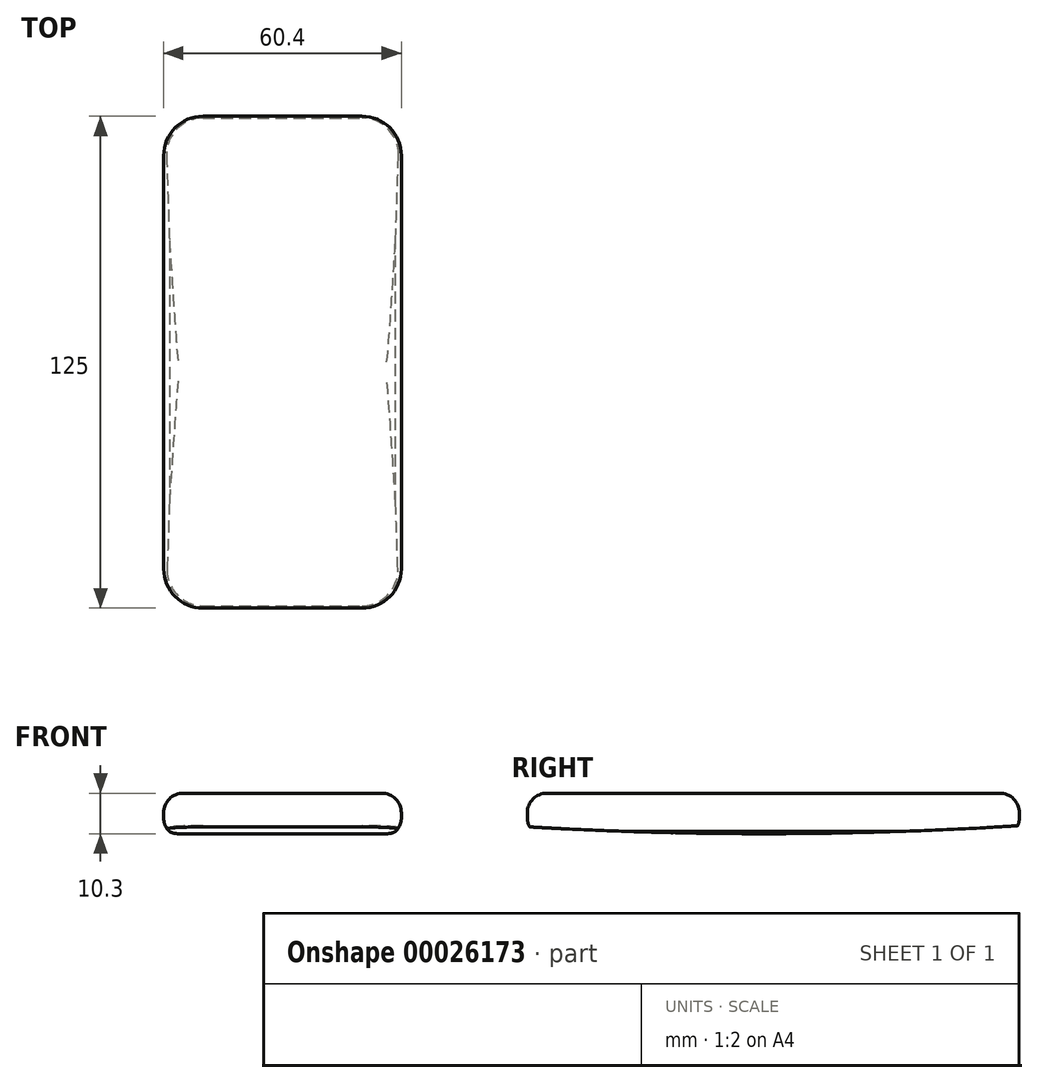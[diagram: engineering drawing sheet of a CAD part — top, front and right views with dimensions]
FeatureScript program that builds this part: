
annotation { "Feature Type Name" : "Feature", "Feature Type Description" : "" }
export const myFeature = defineFeature(function(context is Context, id is Id, definition is map)
    precondition{}
    {
        {
            var Q0;
            Q0=qCreatedBy(makeId("Top.planeOp"),FACE);
            var sketch = newSketch(context, id + "F0", { "sketchPlane" : qUnion([Q0])});
            skLineSegment(sketch, "E0.rect.bottom", {"start": v(-30.2, 62.5) * mm, "end": v(30.2, 62.5) * mm});
            skLineSegment(sketch, "E0.rect.top", {"start": v(-30.2, -62.5) * mm, "end": v(30.2, -62.5) * mm});
            skLineSegment(sketch, "E0.rect.left", {"start": v(-30.2, 62.5) * mm, "end": v(-30.2, -62.5) * mm});
            skLineSegment(sketch, "E0.rect.right", {"start": v(30.2, 62.5) * mm, "end": v(30.2, -62.5) * mm});
            skPoint(sketch, "E0.rect.middle", {"position": v(0, 0) * mm});
            skSolve(sketch);
        }
        {
            var Q0;
            Q0=makeQuery(id+"F0.imprint","IMPRINT",FACE,{"disambiguationData":[TD([[makeQuery(id+"F0.imprint","IMPRINT",EDGE,{"derivedFrom":sQuery(id+"F0.wireOp",EDGE,"E0.rect.bottom")}),-1.0]])]});
            extrude(context, id + "F1", {"entities" : qUnion([Q0]), "depth" : 10.3 * mm});
        }
        {
            var Q0;
            Q0=makeQuery(id+"F1.opExtrude","SWEPT_EDGE",EDGE,{"disambiguationData":[OSD([sQuery(id+"F0.wireOp",EDGE,"E0.rect.bottom"),sQuery(id+"F0.wireOp",EDGE,"E0.rect.left")])]});
            var Q1;
            Q1=makeQuery(id+"F1.opExtrude","SWEPT_EDGE",EDGE,{"disambiguationData":[OSD([sQuery(id+"F0.wireOp",EDGE,"E0.rect.top"),sQuery(id+"F0.wireOp",EDGE,"E0.rect.left")])]});
            var Q2;
            Q2=makeQuery(id+"F1.opExtrude","SWEPT_EDGE",EDGE,{"disambiguationData":[OSD([sQuery(id+"F0.wireOp",EDGE,"E0.rect.top"),sQuery(id+"F0.wireOp",EDGE,"E0.rect.right")])]});
            var Q3;
            Q3=makeQuery(id+"F1.opExtrude","SWEPT_EDGE",EDGE,{"disambiguationData":[OSD([sQuery(id+"F0.wireOp",EDGE,"E0.rect.bottom"),sQuery(id+"F0.wireOp",EDGE,"E0.rect.right")])]});
            fillet(context, id + "F2", {"entities" : qUnion([Q0, Q1, Q2, Q3]), "radius" : 10 * mm, "tangentPropagation" : true, "allowEdgeOverflow" : false});
        }
        {
            var Q0;
            Q0=makeQuery(id+"F1.opExtrude","CAP_FACE",FACE,{"disambiguationData":[OSD([sQuery(id+"F0.wireOp",EDGE,"E0.rect.bottom"),sQuery(id+"F0.wireOp",EDGE,"E0.rect.top"),sQuery(id+"F0.wireOp",EDGE,"E0.rect.left"),sQuery(id+"F0.wireOp",EDGE,"E0.rect.right")])],"isStart":true});
            chamfer(context, id + "F3", {"entities" : qUnion([Q0]), "width" : 2 * mm, "tangentPropagation" : true});
        }
        {
            var Q0;
            Q0=makeQuery(id+"F1.opExtrude","SWEPT_FACE",FACE,{"disambiguationData":[OSD([sQuery(id+"F0.wireOp",EDGE,"E0.rect.left")])]});
            var Q1;
            Q1=makeQuery(id+"F2.opFillet","BLEND_FACE",FACE,{"disambiguationData":[OSD([sQuery(id+"F0.wireOp",EDGE,"E0.rect.bottom"),sQuery(id+"F0.wireOp",EDGE,"E0.rect.left")])]});
            var Q2;
            Q2=makeQuery(id+"F2.opFillet","BLEND_FACE",FACE,{"disambiguationData":[OSD([sQuery(id+"F0.wireOp",EDGE,"E0.rect.top"),sQuery(id+"F0.wireOp",EDGE,"E0.rect.left")])]});
            fillet(context, id + "F4", {"entities" : qUnion([Q0, Q1, Q2]), "radius" : 5 * mm, "tangentPropagation" : true, "allowEdgeOverflow" : false});
        }
        {
            var Q0;
            Q0=makeQuery(id+"F3.opChamfer","BLEND_FACE",FACE,{"disambiguationData":[OSD([sQuery(id+"F0.wireOp",EDGE,"E0.rect.right")])]});
            var Q1;
            {var subQ0=sQuery(id+"F0.wireOp",EDGE,"E0.rect.right");Q1=makeQuery(id+"F4.opFillet","BLEND_EDGE",EDGE,{"blendedFrom":[makeQuery(id+"F1.opExtrude","CAP_EDGE",EDGE,{"disambiguationData":[OSD([subQ0])],"isStart":false}),makeQuery(id+"F1.opExtrude","SWEPT_FACE",FACE,{"disambiguationData":[OSD([subQ0])]})],"blendedInto":[makeQuery(id+"F1.opExtrude","SWEPT_FACE",FACE,{"disambiguationData":[OSD([subQ0])]})]});}
            var Q2;
            {var subQ0=sQuery(id+"F0.wireOp",EDGE,"E0.rect.right");Q2=makeQuery(id+"F3.opChamfer","BLEND_EDGE",EDGE,{"blendedFrom":[makeQuery(id+"F1.opExtrude","CAP_EDGE",EDGE,{"disambiguationData":[OSD([subQ0])],"isStart":true}),makeQuery(id+"F1.opExtrude","SWEPT_FACE",FACE,{"disambiguationData":[OSD([subQ0])]})],"blendedInto":[makeQuery(id+"F1.opExtrude","SWEPT_FACE",FACE,{"disambiguationData":[OSD([subQ0])]})]});}
            var Q3;
            Q3=makeQuery(id+"F4.opFillet","BLEND_FACE",FACE,{"disambiguationData":[OSD([sQuery(id+"F0.wireOp",EDGE,"E0.rect.right")])]});
            var Q4;
            {var subQ0=sQuery(id+"F0.wireOp",EDGE,"E0.rect.bottom");var subQ1=sQuery(id+"F0.wireOp",EDGE,"E0.rect.top");var subQ2=sQuery(id+"F0.wireOp",EDGE,"E0.rect.left");var subQ3=sQuery(id+"F0.wireOp",EDGE,"E0.rect.right");Q4=makeQuery(id+"F4.opFillet","BLEND_FACE",FACE,{"disambiguationData":[OSD([subQ0,subQ1,subQ2,subQ3]),TDD([makeQuery(id+"F2.opFillet","BLEND_EDGE",EDGE,{"blendedFrom":[makeQuery(id+"F1.opExtrude","SWEPT_EDGE",EDGE,{"disambiguationData":[OSD([subQ0,subQ3])]}),makeQuery(id+"F1.opExtrude","CAP_FACE",FACE,{"disambiguationData":[OSD([subQ0,subQ1,subQ2,subQ3])],"isStart":false})],"blendedInto":[makeQuery(id+"F1.opExtrude","CAP_FACE",FACE,{"disambiguationData":[OSD([subQ0,subQ1,subQ2,subQ3])],"isStart":false})]})])]});}
            var Q5;
            Q5=makeQuery(id+"F2.opFillet","BLEND_FACE",FACE,{"disambiguationData":[OSD([sQuery(id+"F0.wireOp",EDGE,"E0.rect.bottom"),sQuery(id+"F0.wireOp",EDGE,"E0.rect.right")])]});
            var Q6;
            {var subQ0=sQuery(id+"F0.wireOp",EDGE,"E0.rect.bottom");var subQ1=sQuery(id+"F0.wireOp",EDGE,"E0.rect.top");var subQ2=sQuery(id+"F0.wireOp",EDGE,"E0.rect.left");var subQ3=sQuery(id+"F0.wireOp",EDGE,"E0.rect.right");Q6=makeQuery(id+"F3.opChamfer","BLEND_FACE",FACE,{"disambiguationData":[OSD([subQ0,subQ1,subQ2,subQ3]),TDD([makeQuery(id+"F2.opFillet","BLEND_EDGE",EDGE,{"blendedFrom":[makeQuery(id+"F1.opExtrude","SWEPT_EDGE",EDGE,{"disambiguationData":[OSD([subQ0,subQ3])]}),makeQuery(id+"F1.opExtrude","CAP_FACE",FACE,{"disambiguationData":[OSD([subQ0,subQ1,subQ2,subQ3])],"isStart":true})],"blendedInto":[makeQuery(id+"F1.opExtrude","CAP_FACE",FACE,{"disambiguationData":[OSD([subQ0,subQ1,subQ2,subQ3])],"isStart":true})]})])]});}
            var Q7;
            {var subQ0=sQuery(id+"F0.wireOp",EDGE,"E0.rect.top");var subQ1=sQuery(id+"F0.wireOp",EDGE,"E0.rect.right");Q7=makeQuery(id+"F3.opChamfer","BLEND_EDGE",EDGE,{"blendedFrom":[makeQuery(id+"F2.opFillet","BLEND_EDGE",EDGE,{"blendedFrom":[makeQuery(id+"F1.opExtrude","SWEPT_EDGE",EDGE,{"disambiguationData":[OSD([subQ0,subQ1])]}),makeQuery(id+"F1.opExtrude","CAP_FACE",FACE,{"disambiguationData":[OSD([sQuery(id+"F0.wireOp",EDGE,"E0.rect.bottom"),subQ0,sQuery(id+"F0.wireOp",EDGE,"E0.rect.left"),subQ1])],"isStart":true})],"blendedInto":[makeQuery(id+"F1.opExtrude","CAP_FACE",FACE,{"disambiguationData":[OSD([sQuery(id+"F0.wireOp",EDGE,"E0.rect.bottom"),subQ0,sQuery(id+"F0.wireOp",EDGE,"E0.rect.left"),subQ1])],"isStart":true})]}),makeQuery(id+"F2.opFillet","BLEND_FACE",FACE,{"disambiguationData":[OSD([subQ0,subQ1])]})],"blendedInto":[makeQuery(id+"F2.opFillet","BLEND_FACE",FACE,{"disambiguationData":[OSD([subQ0,subQ1])]})]});}
            var Q8;
            Q8=makeQuery(id+"F2.opFillet","BLEND_FACE",FACE,{"disambiguationData":[OSD([sQuery(id+"F0.wireOp",EDGE,"E0.rect.top"),sQuery(id+"F0.wireOp",EDGE,"E0.rect.right")])]});
            var Q9;
            {var subQ0=sQuery(id+"F0.wireOp",EDGE,"E0.rect.top");var subQ1=sQuery(id+"F0.wireOp",EDGE,"E0.rect.right");var subQ2=makeQuery(id+"F1.opExtrude","CAP_FACE",FACE,{"disambiguationData":[OSD([sQuery(id+"F0.wireOp",EDGE,"E0.rect.bottom"),subQ0,sQuery(id+"F0.wireOp",EDGE,"E0.rect.left"),subQ1])],"isStart":false});Q9=makeQuery(id+"F4.opFillet","BLEND_EDGE",EDGE,{"blendedFrom":[makeQuery(id+"F2.opFillet","BLEND_EDGE",EDGE,{"blendedFrom":[makeQuery(id+"F1.opExtrude","SWEPT_EDGE",EDGE,{"disambiguationData":[OSD([subQ0,subQ1])]}),subQ2],"blendedInto":[subQ2]}),subQ2],"blendedInto":[subQ2]});}
            fillet(context, id + "F5", {"entities" : qUnion([Q0, Q1, Q2, Q3, Q4, Q5, Q6, Q7, Q8, Q9]), "radius" : 5 * mm, "tangentPropagation" : true, "allowEdgeOverflow" : false});
        }
        {
            var Q0;
            Q0=qCreatedBy(makeId("Right.planeOp"),FACE);
            var sketch = newSketch(context, id + "F6", { "sketchPlane" : qUnion([Q0])});
            skArc(sketch, "E1", {"start": v(-98.01, 4.44) * mm, "mid": v(0.01, 0) * mm, "end": v(98.01, 4.9) * mm});
            skLineSegment(sketch, "E2", {"start": v(98.01, 4.9) * mm, "end": v(98.01, -23.82) * mm});
            skLineSegment(sketch, "E3", {"start": v(98.01, -23.82) * mm, "end": v(-98.01, 4.44) * mm});
            skSolve(sketch);
        }
        {
            var Q0;
            Q0=makeQuery(id+"F6.imprint","IMPRINT",FACE,{"disambiguationData":[TD([[makeQuery(id+"F6.imprint","IMPRINT",EDGE,{"derivedFrom":sQuery(id+"F6.wireOp",EDGE,"E1")}),-1.0]])]});
            extrude(context, id + "F7", {"entities" : qUnion([Q0]), "operationType" : NewBodyOperationType.REMOVE, "endBound" : BoundingType.SYMMETRIC, "oppositeDirection" : true, "depth" : 80 * mm});
        }
    });
